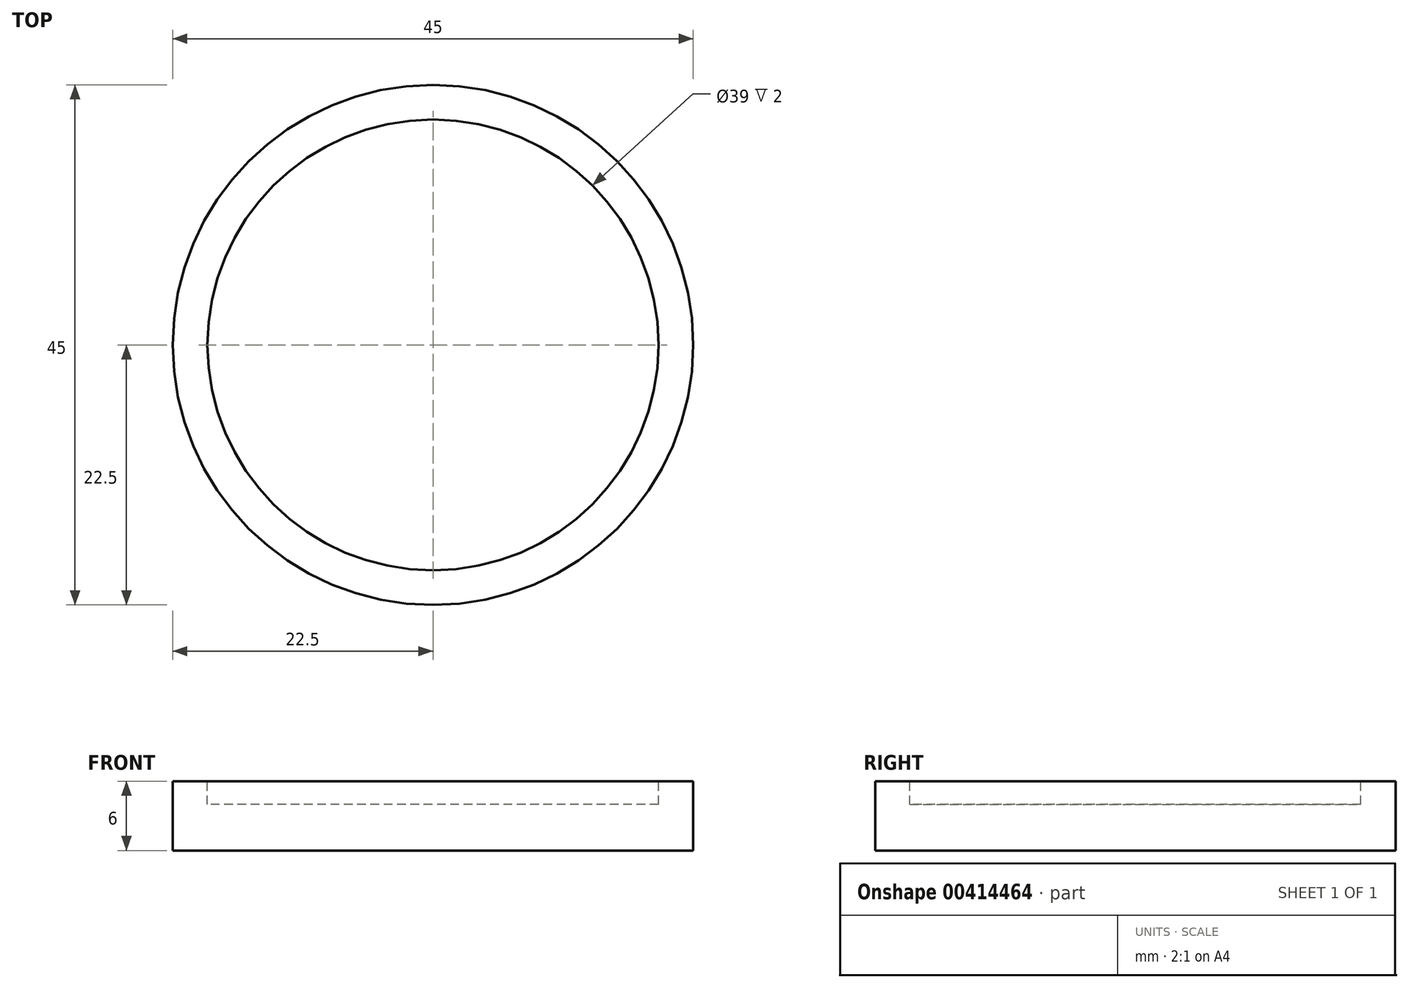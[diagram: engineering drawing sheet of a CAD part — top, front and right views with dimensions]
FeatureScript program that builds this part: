
annotation { "Feature Type Name" : "Feature", "Feature Type Description" : "" }
export const myFeature = defineFeature(function(context is Context, id is Id, definition is map)
    precondition{}
    {
        {
            var Q0;
            Q0=qCreatedBy(makeId("Front.planeOp"),FACE);
            var sketch = newSketch(context, id + "F0", { "sketchPlane" : qUnion([Q0])});
            skLineSegment(sketch, "E0", {"start": v(0, 0) * mm, "end": v(-22.5, 0) * mm});
            skLineSegment(sketch, "E1", {"start": v(-22.5, 0) * mm, "end": v(-22.5, 6) * mm});
            skLineSegment(sketch, "E2", {"start": v(-22.5, 6) * mm, "end": v(-19.5, 6) * mm});
            skLineSegment(sketch, "E3", {"start": v(-19.5, 6) * mm, "end": v(-19.5, 4) * mm});
            skLineSegment(sketch, "E4", {"start": v(-19.5, 4) * mm, "end": v(0, 4) * mm});
            skLineSegment(sketch, "E5", {"start": v(0, 4) * mm, "end": v(0, 0) * mm});
            skSolve(sketch);
        }
        {
            var Q0;
            Q0 = qSketchRegion(id + "F0", true);
            var Q1;
            Q1=sQuery(id+"F0.wireOp",EDGE,"E5");
            revolve(context, id + "F1", {"entities" : qUnion([Q0]), "axis" : qUnion([Q1]), "revolveType" : RevolveType.FULL});
        }
    });
